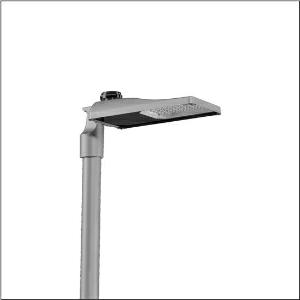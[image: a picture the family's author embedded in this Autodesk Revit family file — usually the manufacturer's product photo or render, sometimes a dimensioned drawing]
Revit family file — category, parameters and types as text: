
# Revit family: streetlight_sl_31_mini___st1_0a_5xh6d35n08ga_9230
name_source: partatom
category: Lighting Fixtures
units: mm (PartAtom-declared; Revit-internal decimal feet)

## family parameters
Cut with Voids When Loaded = No
Host = Face
Light Source = No
Part Type = Normal
Room Calculation Point = No
Round Connector Dimension = Use Diameter
Shared = No

## types (1)
- --- (1 x LED, 5710 lm, 37.3 W, 3000K)
    Apparent Load = 37 VA
    CIE Flux Codes = 37 72 97 100 100
    Color Rendering = 70
    Color Temperature = 3000K
    Default Elevation = 1800 mm
    Description = Streetlight SL 31 mini, mast luminaire, primary light control with lens, of PMMA, primary optical cover: cover, of toughened safety glass, transparent, light distribution: ST1.0a, light emission: direct distribution, primary light characteristic: asymmetric, installation type: post-top, side-entry, LED, High Power LED, rated luminous flux: 5.710lm, luminous efficacy: 153lm/W, light colour: 730, colour temperature: 3000K, control: presetting dimming linear, flexible luminous flux parameterisation, time-dependent luminous flux control, constant luminous flux control, intelligent temperature release in ECG and LED module, overheat protection, with cable H07RN-F 3x 1.5mm², mains connection: 220..240V, AC, 50/60Hz, connection cable pre-assembled, cable length: 6,5m, start of lifetime: 37W, end of service life: 39W, reduction: 18W, luminaire housing, of diecast aluminium, powder-coated, Siteco® metallic grey (DB 702S), corrosivity category C5 high according to DIN EN ISO 12944, no sealing on luminaire upper side, inclination: -15°..+20° (post-top) | -20°..+20° (side-entry), adjustable in 5° steps, mast flange (76/60mm) included as standard, multi-level sealing system, sealing non-destructively replaceable, protection rating (complete): IP66, insulation class (complete): insulation class I (protective earthing), certification: CE, ENEC, ENEC+, VDE, UKCA, impact resistance: IK09, permissible operating ambient temperature for outdoor applications: -40..+50°C, standard-compliant lighting for roads and squares, packaging unit: 1 piece

Light Distribution: ST1.0a
    Height = 76 mm
    Lamp = 1 x LED
    Lamp Light Flux = 5710 lm
    Lamp Power = 37.3 W
    Lamp count = 1
    Length = 547 mm
    Luminous efficacy = 153 lm/W
    Manufacturer = Siteco
    ModVariant = No
    Model = 5XH6D35N08GA
    Number of Poles = 1
    OnlyDefault = Yes
    Power Factor = 1
    Product Name = Streetlight SL 31 mini | ST1.0a
    Product group = mast luminaire | pylon top
    ProductGroupID = 6100
    Protection Class = Protection class I
    Protection Degree = IP 66
    RLX_Detail_Level = 1
    RLX_Emergency_Light_Flux = 0 lm
    RLX_Emergency_Type = 0
    RLX_Emergency_Type_DB = No
    RlxData = <blob elided: 40361 chars, md5=5731fdee>
    Socket = socket
    Standby Power = 0 W
    System Light Flux = 5710 lm
    System Power = 37 W
    Type Comments = factory setting: luminous flux: 100 % | dim-lin: 254 | 386 mA
    Type Image = l_1300322.jpg
    URL = http://relux.com
    VarID = @adj_011559
    Voltage = 0 V
    Weight = 0.00 kg
    Width = 265 mm

## geometry (parser evidence)
native form markers: Blend x4, Sweep x9
no freeform markers — native parametric forms only
